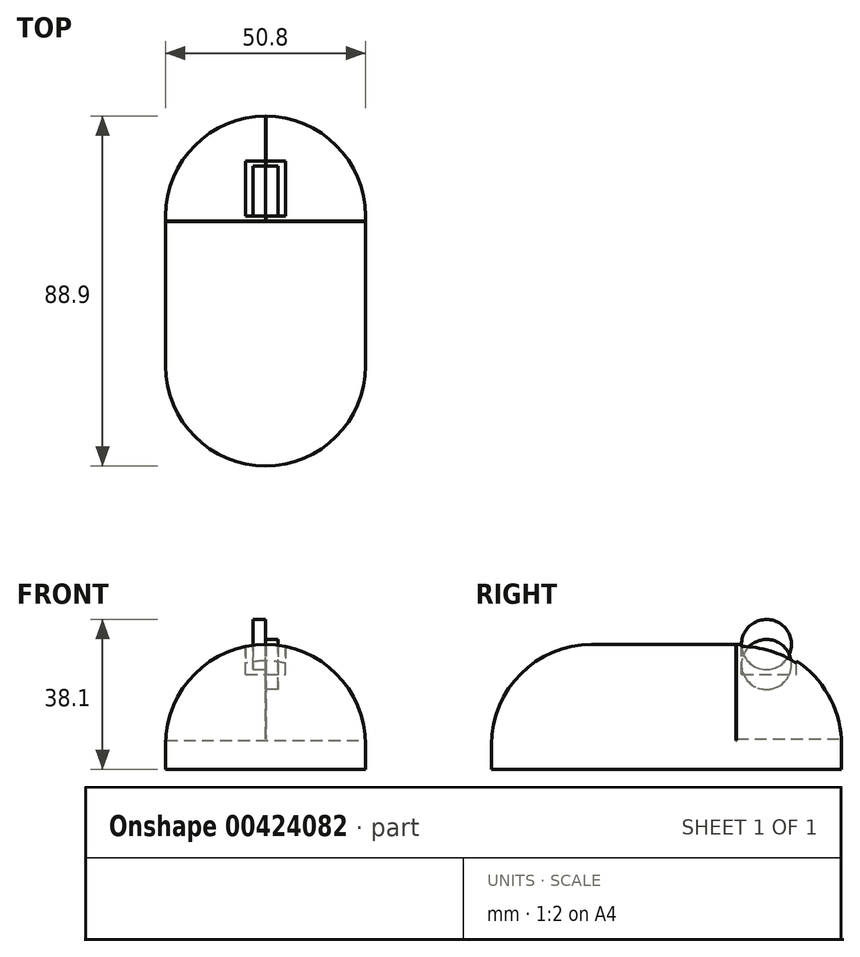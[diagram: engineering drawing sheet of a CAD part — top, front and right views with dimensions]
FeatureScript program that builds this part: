
annotation { "Feature Type Name" : "Feature", "Feature Type Description" : "" }
export const myFeature = defineFeature(function(context is Context, id is Id, definition is map)
    precondition{}
    {
        {
            var Q0;
            Q0=qCreatedBy(makeId("Top.planeOp"),FACE);
            var sketch = newSketch(context, id + "F0", { "sketchPlane" : qUnion([Q0])});
            skLineSegment(sketch, "E0.bottom", {"start": v(-5.08, 13.97) * mm, "end": v(5.08, 13.97) * mm});
            skLineSegment(sketch, "E0.top", {"start": v(-5.08, 0) * mm, "end": v(5.08, 0) * mm});
            skLineSegment(sketch, "E0.left", {"start": v(-5.08, 13.97) * mm, "end": v(-5.08, 0) * mm});
            skLineSegment(sketch, "E0.right", {"start": v(5.08, 13.97) * mm, "end": v(5.08, 0) * mm});
            skLineSegment(sketch, "E1", {"start": v(0, 0) * mm, "end": v(0, 0) * mm});
            skLineSegment(sketch, "E2", {"start": v(-5.08, 0) * mm, "end": v(0, 0) * mm});
            skSolve(sketch);
        }
        {
            var Q0;
            Q0=qCreatedBy(makeId("Top.planeOp"),FACE);
            var sketch = newSketch(context, id + "F1", { "sketchPlane" : qUnion([Q0])});
            skLineSegment(sketch, "E3.bottom", {"start": v(-25.4, 0) * mm, "end": v(25.4, 0) * mm});
            skLineSegment(sketch, "E3.top", {"start": v(-25.4, -63.5) * mm, "end": v(25.4, -63.5) * mm});
            skLineSegment(sketch, "E3.left", {"start": v(-25.4, 0) * mm, "end": v(-25.4, -63.5) * mm});
            skLineSegment(sketch, "E3.right", {"start": v(25.4, 0) * mm, "end": v(25.4, -63.5) * mm});
            skPoint(sketch, "E4", {"position": v(-25.4, 0) * mm});
            skPoint(sketch, "E5", {"position": v(25.4, 0) * mm});
            skLineSegment(sketch, "E6", {"start": v(-25.4, 0) * mm, "end": v(0, 0) * mm});
            skLineSegment(sketch, "E7", {"start": v(0, 0) * mm, "end": v(25.4, 0) * mm});
            skLineSegment(sketch, "E8", {"start": v(0, 0) * mm, "end": v(0, 0) * mm});
            skCircle(sketch, "E9", {"center": v(0, 0) * mm, "radius": 25.4 * mm});
            skSolve(sketch);
        }
        {
            var Q0;
            Q0 = qSketchRegion(id + "F1", true);
            extrude(context, id + "F2", {"entities" : qUnion([Q0]), "oppositeDirection" : true, "depth" : 31.75 * mm});
        }
        {
            var Q0;
            Q0 = qSketchRegion(id + "F0", true);
            extrude(context, id + "F3", {"entities" : qUnion([Q0]), "operationType" : NewBodyOperationType.REMOVE, "oppositeDirection" : true, "depth" : 7.62 * mm});
        }
        {
            var Q0;
            Q0=qCreatedBy(makeId("Right.planeOp"),FACE);
            var sketch = newSketch(context, id + "F4", { "sketchPlane" : qUnion([Q0])});
            skCircle(sketch, "E10", {"center": v(0, 0) * mm, "radius": 6.35 * mm});
            skLineSegment(sketch, "E11", {"start": v(0, 0) * mm, "end": v(0, 12.38) * mm, "construction": true});
            skLineSegment(sketch, "E12", {"start": v(10, 12.38) * mm, "end": v(0, 12.38) * mm, "construction": true});
            skLineSegment(sketch, "E13", {"start": v(0, 0) * mm, "end": v(0, -6.35) * mm, "construction": true});
            skSolve(sketch);
        }
        {
            var Q0;
            Q0=makeQuery(id+"F4.imprint","IMPRINT",FACE,{"disambiguationData":[TD([[makeQuery(id+"F4.imprint","IMPRINT",EDGE,{"derivedFrom":sQuery(id+"F4.wireOp",EDGE,"E10")}),1.0]])]});
            extrude(context, id + "F5", {"entities" : qUnion([Q0]), "depth" : 3.17 * mm});
        }
        {
            var Q0;
            Q0 = qSketchRegion(id + "F4", true);
            extrude(context, id + "F6", {"entities" : qUnion([Q0]), "oppositeDirection" : true, "depth" : 3.17 * mm});
        }
        {
            var Q0;
            Q0=makeQuery(id+"F2.opExtrude","CAP_EDGE",EDGE,{"disambiguationData":[OSD([sQuery(id+"F1.wireOp",EDGE,"E9")])],"isStart":true});
            var Q1;
            Q1=makeQuery(id+"F2.opExtrude","CAP_EDGE",EDGE,{"disambiguationData":[OSD([sQuery(id+"F1.wireOp",EDGE,"E3.right")])],"isStart":true});
            var Q2;
            Q2=makeQuery(id+"F2.opExtrude","CAP_EDGE",EDGE,{"disambiguationData":[OSD([sQuery(id+"F1.wireOp",EDGE,"E3.left")])],"isStart":true});
            fillet(context, id + "F7", {"entities" : qUnion([Q0, Q1, Q2]), "radius" : 25.4 * mm, "tangentPropagation" : true, "allowEdgeOverflow" : false});
        }
        {
            var Q0;
            Q0=makeQuery(id+"F2.opExtrude","SWEPT_BODY",BODY,{"disambiguationData":[OSD([sQuery(id+"F1.wireOp",EDGE,"E3.top"),sQuery(id+"F1.wireOp",EDGE,"E3.left"),sQuery(id+"F1.wireOp",EDGE,"E3.right"),sQuery(id+"F1.wireOp",EDGE,"E9")])]});
            var Q1;
            Q1=makeQuery(id+"F2.opExtrude","SWEPT_FACE",FACE,{"disambiguationData":[OSD([sQuery(id+"F1.wireOp",EDGE,"E3.top")])]});
            transform(context, id + "F8", {"entities" : qUnion([Q0]), "transformType" : TransformType.TRANSLATION_DISTANCE, "transformDirection" : qUnion([Q1]), "distance" : 6.35 * mm, "makeCopy" : false});
        }
        {
            var Q0;
            Q0=makeQuery(id+"F7.opFillet","BLEND_EDGE",EDGE,{"blendedFrom":[makeQuery(id+"F2.opExtrude","CAP_EDGE",EDGE,{"disambiguationData":[OSD([sQuery(id+"F1.wireOp",EDGE,"E9")])],"isStart":true}),makeQuery(id+"F3.boolean.opBoolean","COPY",FACE,{"derivedFrom":makeQuery(id+"F3.opExtrude","SWEPT_FACE",FACE,{"disambiguationData":[OSD([sQuery(id+"F0.wireOp",EDGE,"E0.bottom")])]})})],"blendedInto":[makeQuery(id+"F3.boolean.opBoolean","COPY",FACE,{"derivedFrom":makeQuery(id+"F3.opExtrude","SWEPT_FACE",FACE,{"disambiguationData":[OSD([sQuery(id+"F0.wireOp",EDGE,"E0.bottom")])]})})]});
            cPoint(context, id + "F9", {"entities" : qUnion([Q0]), "parameter" : 0.5});
        }
        {
            var Q0;
            Q0=makeQuery(id+"F5.opExtrude","SWEPT_BODY",BODY,{"disambiguationData":[OSD([sQuery(id+"F4.wireOp",EDGE,"E10")])]});
            var Q1;
            Q1=qCreatedBy(makeId("Origin.pointOp"),VERTEX);
            var Q2;
            Q2 = qCreatedBy(id + "F9" ,VERTEX);
            var Q3;
            Q3=makeQuery(id+"F3.boolean.opBoolean","COPY",FACE,{"derivedFrom":makeQuery(id+"F3.opExtrude","CAP_FACE",FACE,{"disambiguationData":[OSD([sQuery(id+"F0.wireOp",EDGE,"E0.bottom"),sQuery(id+"F0.wireOp",EDGE,"E0.top"),sQuery(id+"F0.wireOp",EDGE,"E0.left"),sQuery(id+"F0.wireOp",EDGE,"E0.right"),sQuery(id+"F0.wireOp",EDGE,"E2")])],"isStart":false})});
            transform(context, id + "F10", {"entities" : qUnion([Q0]), "transformType" : TransformType.TRANSLATION_DISTANCE, "transformDirection" : qUnion([Q3]), "distance" : 5.08 * mm, "oppositeDirection" : true, "makeCopy" : false});
        }
        {
            var Q0;
            Q0=makeQuery(id+"F2.opExtrude","SWEPT_FACE",FACE,{"disambiguationData":[OSD([sQuery(id+"F1.wireOp",EDGE,"E3.top")])]});
            cPlane(context, id + "F11", {"entities" : qUnion([Q0]), "cplaneType" : CPlaneType.OFFSET, "offset" : 63.5 * mm, "oppositeDirection" : true, "width" : 152.4 * mm, "height" : 152.4 * mm});
        }
        {
            var Q0;
            Q0=qCreatedBy(id+"F11.planeOp",FACE);
            var sketch = newSketch(context, id + "F12", { "sketchPlane" : qUnion([Q0])});
            skLineSegment(sketch, "E14.bottom", {"start": v(-25.36, 0.24) * mm, "end": v(25.44, 0.24) * mm});
            skLineSegment(sketch, "E14.top", {"start": v(-25.36, -24.4) * mm, "end": v(25.44, -24.4) * mm});
            skLineSegment(sketch, "E14.left", {"start": v(-25.36, 0.24) * mm, "end": v(-25.36, -24.4) * mm});
            skLineSegment(sketch, "E14.right", {"start": v(25.44, 0.24) * mm, "end": v(25.44, -24.4) * mm});
            skSolve(sketch);
        }
        {
            var Q0;
            Q0 = qSketchRegion(id + "F12", true);
            extrude(context, id + "F13", {"entities" : qUnion([Q0]), "depth" : 0.13 * mm});
        }
        {
            var Q0;
            Q0=makeQuery(id+"F13.opExtrude","SWEPT_BODY",BODY,{"disambiguationData":[OSD([sQuery(id+"F12.wireOp",EDGE,"E14.bottom"),sQuery(id+"F12.wireOp",EDGE,"E14.top"),sQuery(id+"F12.wireOp",EDGE,"E14.left"),sQuery(id+"F12.wireOp",EDGE,"E14.right")])]});
            var Q1;
            Q1=makeQuery(id+"F2.opExtrude","SWEPT_FACE",FACE,{"disambiguationData":[OSD([sQuery(id+"F1.wireOp",EDGE,"E3.top")])]});
            transform(context, id + "F14", {"entities" : qUnion([Q0]), "transformType" : TransformType.TRANSLATION_DISTANCE, "transformDirection" : qUnion([Q1]), "distance" : 1.27 * mm, "makeCopy" : false});
        }
        {
            var Q0;
            Q0=makeQuery(id+"F13.opExtrude","SWEPT_BODY",BODY,{"disambiguationData":[OSD([sQuery(id+"F12.wireOp",EDGE,"E14.bottom"),sQuery(id+"F12.wireOp",EDGE,"E14.top"),sQuery(id+"F12.wireOp",EDGE,"E14.left"),sQuery(id+"F12.wireOp",EDGE,"E14.right")])]});
            var Q1;
            Q1=makeQuery(id+"F2.opExtrude","SWEPT_BODY",BODY,{"disambiguationData":[OSD([sQuery(id+"F1.wireOp",EDGE,"E3.top"),sQuery(id+"F1.wireOp",EDGE,"E3.left"),sQuery(id+"F1.wireOp",EDGE,"E3.right"),sQuery(id+"F1.wireOp",EDGE,"E9")])]});
            booleanBodies(context, id + "F15", {"operationType" : BooleanOperationType.SUBTRACTION, "tools" : qUnion([Q0]), "targets" : qUnion([Q1])});
        }
        {
            var Q0;
            Q0=qCreatedBy(makeId("Right.planeOp"),FACE);
            var sketch = newSketch(context, id + "F16", { "sketchPlane" : qUnion([Q0])});
            skLineSegment(sketch, "E15.bottom", {"start": v(-7.54, 5.98) * mm, "end": v(21.55, 5.98) * mm});
            skLineSegment(sketch, "E15.top", {"start": v(-7.54, -24) * mm, "end": v(21.55, -24) * mm});
            skLineSegment(sketch, "E15.left", {"start": v(-7.54, 5.98) * mm, "end": v(-7.54, -24) * mm});
            skLineSegment(sketch, "E15.right", {"start": v(21.55, 5.98) * mm, "end": v(21.55, -24) * mm});
            skSolve(sketch);
        }
        {
            var Q0;
            Q0 = qSketchRegion(id + "F16", true);
            extrude(context, id + "F17", {"entities" : qUnion([Q0]), "depth" : 0.13 * mm});
        }
        {
            var Q0;
            Q0=makeQuery(id+"F17.opExtrude","SWEPT_BODY",BODY,{"disambiguationData":[OSD([sQuery(id+"F16.wireOp",EDGE,"E15.bottom"),sQuery(id+"F16.wireOp",EDGE,"E15.top"),sQuery(id+"F16.wireOp",EDGE,"E15.left"),sQuery(id+"F16.wireOp",EDGE,"E15.right")])]});
            var Q1;
            Q1=makeQuery(id+"F2.opExtrude","SWEPT_BODY",BODY,{"disambiguationData":[OSD([sQuery(id+"F1.wireOp",EDGE,"E3.top"),sQuery(id+"F1.wireOp",EDGE,"E3.left"),sQuery(id+"F1.wireOp",EDGE,"E3.right"),sQuery(id+"F1.wireOp",EDGE,"E9")])]});
            booleanBodies(context, id + "F18", {"operationType" : BooleanOperationType.SUBTRACTION, "tools" : qUnion([Q0]), "targets" : qUnion([Q1])});
        }
        {
            var Q0;
            Q0=makeQuery(id+"F7.opFillet","BLEND_EDGE",EDGE,{"blendedFrom":[makeQuery(id+"F2.opExtrude","CAP_EDGE",EDGE,{"disambiguationData":[OSD([sQuery(id+"F1.wireOp",EDGE,"E3.left")])],"isStart":true}),makeQuery(id+"F2.opExtrude","SWEPT_FACE",FACE,{"disambiguationData":[OSD([sQuery(id+"F1.wireOp",EDGE,"E3.top")])]})],"blendedInto":[makeQuery(id+"F2.opExtrude","SWEPT_FACE",FACE,{"disambiguationData":[OSD([sQuery(id+"F1.wireOp",EDGE,"E3.top")])]})]});
            fillet(context, id + "F19", {"entities" : qUnion([Q0]), "radius" : 25.4 * mm, "tangentPropagation" : true, "allowEdgeOverflow" : false});
        }
    });
